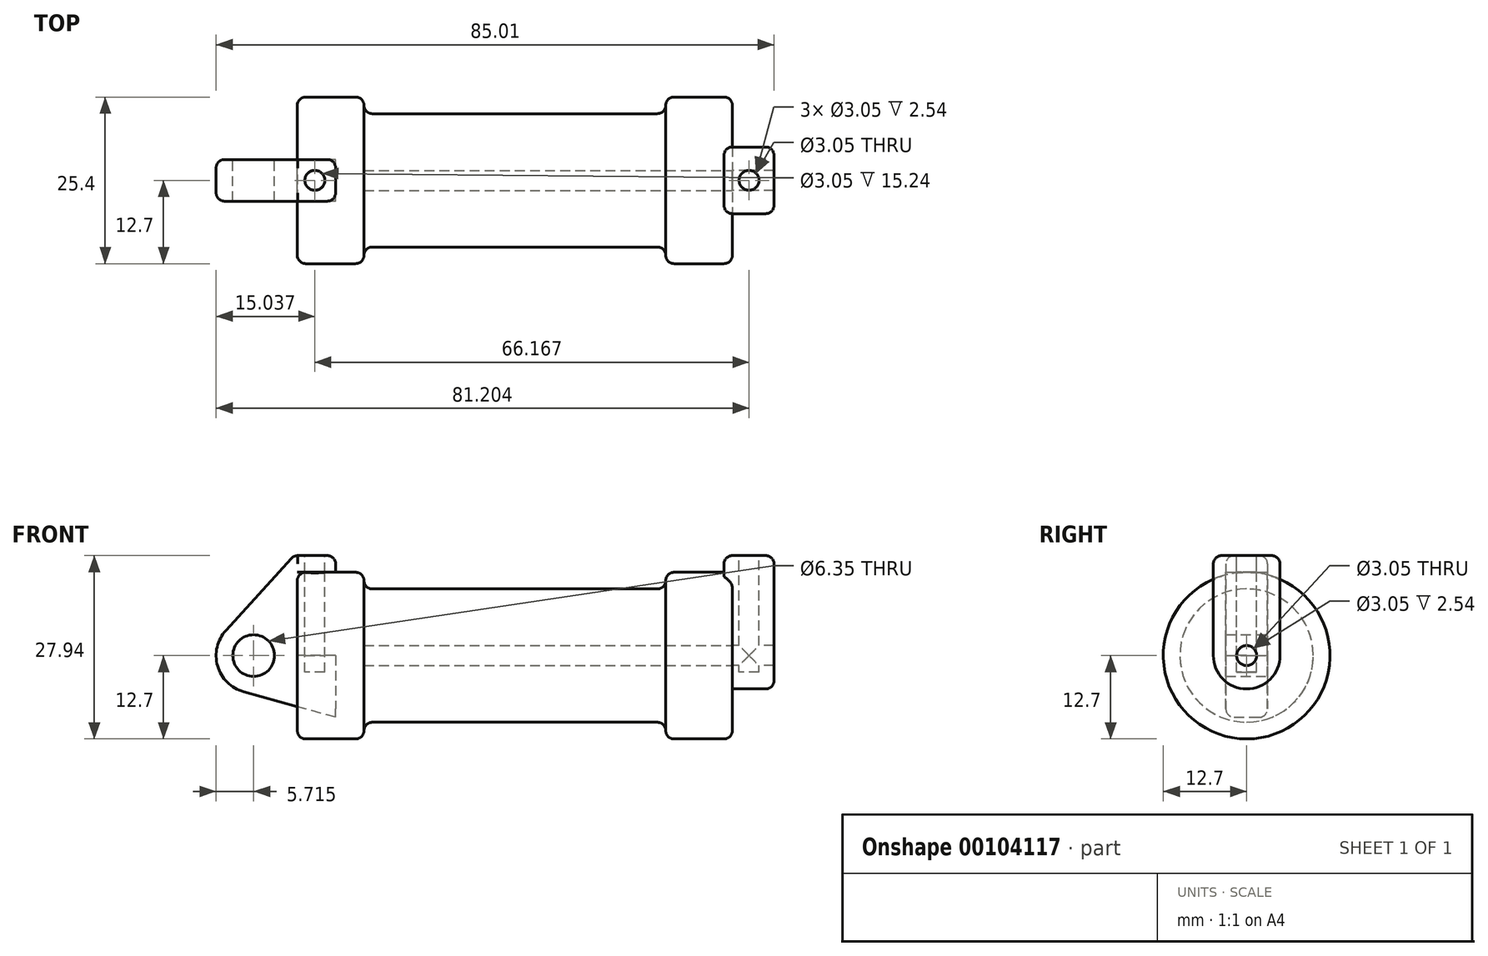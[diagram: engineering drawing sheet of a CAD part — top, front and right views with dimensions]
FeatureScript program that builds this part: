
annotation { "Feature Type Name" : "Feature", "Feature Type Description" : "" }
export const myFeature = defineFeature(function(context is Context, id is Id, definition is map)
    precondition{}
    {
        {
            var Q0;
            Q0=qCreatedBy(makeId("Front.planeOp"),FACE);
            var sketch = newSketch(context, id + "F0", { "sketchPlane" : qUnion([Q0])});
            skLineSegment(sketch, "E0", {"start": v(0, 0) * mm, "end": v(0, 12.7) * mm});
            skLineSegment(sketch, "E1", {"start": v(0, 12.7) * mm, "end": v(10.16, 12.7) * mm});
            skLineSegment(sketch, "E2", {"start": v(10.16, 12.7) * mm, "end": v(10.16, 10.16) * mm});
            skLineSegment(sketch, "E3", {"start": v(10.16, 10.16) * mm, "end": v(56.13, 10.16) * mm});
            skLineSegment(sketch, "E4", {"start": v(56.13, 10.16) * mm, "end": v(56.13, 12.7) * mm});
            skLineSegment(sketch, "E5", {"start": v(56.13, 12.7) * mm, "end": v(66.3, 12.7) * mm});
            skLineSegment(sketch, "E6", {"start": v(66.3, 12.7) * mm, "end": v(66.3, 0) * mm});
            skLineSegment(sketch, "E7", {"start": v(66.3, 0) * mm, "end": v(0, 0) * mm});
            skLineSegment(sketch, "E8", {"start": v(5.84, 15.24) * mm, "end": v(-0.5, 15.24) * mm});
            skLineSegment(sketch, "E9", {"start": v(-0.5, 15.24) * mm, "end": v(-10.88, 3.85) * mm});
            skLineSegment(sketch, "E10", {"start": v(0, 0) * mm, "end": v(-6.65, 0) * mm});
            skCircle(sketch, "E11", {"center": v(-6.65, 0) * mm, "radius": 5.72 * mm});
            skCircle(sketch, "E12", {"center": v(-6.65, 0) * mm, "radius": 3.18 * mm});
            skLineSegment(sketch, "E13", {"start": v(5.84, 15.24) * mm, "end": v(5.84, -9.4) * mm});
            skLineSegment(sketch, "E14", {"start": v(5.84, -9.4) * mm, "end": v(-8.18, -5.5) * mm});
            skSolve(sketch);
        }
        {
            var Q0;
            {var subQ0=sQuery(id+"F0.wireOp",EDGE,"E2");Q0=makeQuery(id+"F0.imprint","IMPRINT",FACE,{"disambiguationData":[TD([[makeQuery(id+"F0.imprint","IMPRINT",EDGE,{"derivedFrom":subQ0}),-1.0]])]});}
            var Q1;
            {var subQ0=sQuery(id+"F0.wireOp",EDGE,"E0");Q1=makeQuery(id+"F0.imprint","IMPRINT",FACE,{"disambiguationData":[TD([[makeQuery(id+"F0.imprint","IMPRINT",EDGE,{"derivedFrom":subQ0}),-1.0]])]});}
            var Q2;
            Q2=sQuery(id+"F0.wireOp",EDGE,"E7");
            revolve(context, id + "F1", {"entities" : qUnion([Q0, Q1]), "axis" : qUnion([Q2]), "revolveType" : RevolveType.FULL});
        }
        {
            var Q0;
            Q0=makeQuery(id+"F1.opRevolve","SWEPT_FACE",FACE,{"disambiguationData":[OSD([sQuery(id+"F0.wireOp",EDGE,"E6")])]});
            var sketch = newSketch(context, id + "F2", { "sketchPlane" : qUnion([Q0])});
            skCircle(sketch, "E15", {"center": v(0, 0) * mm, "radius": 1.52 * mm});
            skCircle(sketch, "E16", {"center": v(0, 0) * mm, "radius": 5.08 * mm});
            skLineSegment(sketch, "E17", {"start": v(-5.08, 0) * mm, "end": v(-5.08, 15.24) * mm});
            skLineSegment(sketch, "E18", {"start": v(5.08, 0) * mm, "end": v(5.08, 15.24) * mm});
            skLineSegment(sketch, "E19", {"start": v(-5.08, 15.24) * mm, "end": v(5.08, 15.24) * mm});
            skSolve(sketch);
        }
        {
            var Q0;
            {var subQ0=sQuery(id+"F2.wireOp",EDGE,"E19");Q0=makeQuery(id+"F2.imprint","IMPRINT",FACE,{"disambiguationData":[TD([[makeQuery(id+"F2.imprint","IMPRINT",EDGE,{"derivedFrom":subQ0}),-1.0]])]});}
            var Q1;
            Q1=makeQuery(id+"F2.imprint","IMPRINT",FACE,{"disambiguationData":[TD([[makeQuery(id+"F2.imprint","IMPRINT",EDGE,{"derivedFrom":sQuery(id+"F2.wireOp",EDGE,"E15")}),-1.0]])]});
            var Q2;
            {var subQ0=sQuery(id+"F2.wireOp",EDGE,"E17");var subQ1=sQuery(id+"F2.wireOp",EDGE,"E16");var subQ2=makeQuery(id+"F2.imprint","INTERSECT",VERTEX,{"derivedFrom":[subQ1,subQ0]});Q2=makeQuery(id+"F2.imprint","IMPRINT",FACE,{"disambiguationData":[TD([[makeQuery(id+"F2.imprint","IMPRINT",EDGE,{"disambiguationData":[TD([[subQ2,1.0]])],"derivedFrom":subQ1}),-1.0]])]});}
            extrude(context, id + "F3", {"entities" : qUnion([Q0, Q1, Q2]), "operationType" : NewBodyOperationType.ADD, "oppositeDirection" : true, "depth" : 1.27 * mm});
        }
        {
            var Q0;
            Q0 = qSketchRegion(id + "F2", true);
            extrude(context, id + "F4", {"entities" : qUnion([Q0]), "operationType" : NewBodyOperationType.ADD, "depth" : 6.35 * mm});
        }
        {
            var Q0;
            {var subQ0=sQuery(id+"F2.wireOp",EDGE,"E15");Q0=makeQuery(id+"F4.boolean.opBoolean","SPLIT",FACE,{"disambiguationData":[TD([makeQuery(id+"F4.opExtrude","SWEPT_FACE",FACE,{"disambiguationData":[OSD([subQ0])]})])],"derivedFrom":makeQuery(id+"F3.boolean.opBoolean","MERGE",FACE,{"derivedFrom":[makeQuery(id+"F1.opRevolve","SWEPT_FACE",FACE,{"disambiguationData":[OSD([sQuery(id+"F0.wireOp",EDGE,"E6")])]}),makeQuery(id+"F3.opExtrude","CAP_FACE",FACE,{"disambiguationData":[OSD([subQ0,sQuery(id+"F2.wireOp",EDGE,"E16"),sQuery(id+"F2.wireOp",EDGE,"E17"),sQuery(id+"F2.wireOp",EDGE,"E18"),sQuery(id+"F2.wireOp",EDGE,"E19")])],"isStart":true})]})});}
            var Q1;
            Q1=makeQuery(id+"F1.opRevolve","SWEPT_FACE",FACE,{"disambiguationData":[OSD([sQuery(id+"F0.wireOp",EDGE,"E2")])]});
            extrude(context, id + "F5", {"entities" : qUnion([Q0]), "endBound" : BoundingType.UP_TO_SURFACE, "oppositeDirection" : true, "endBoundEntityFace" : qUnion([Q1]), "depth" : 25.4 * mm});
        }
        {
            var Q0;
            {var subQ0=sQuery(id+"F2.wireOp",EDGE,"E19");Q0=makeQuery(id+"F4.boolean.opBoolean","MERGE",FACE,{"derivedFrom":[makeQuery(id+"F3.opExtrude","SWEPT_FACE",FACE,{"disambiguationData":[OSD([subQ0])]}),makeQuery(id+"F4.opExtrude","SWEPT_FACE",FACE,{"disambiguationData":[OSD([subQ0])]})]});}
            var sketch = newSketch(context, id + "F6", { "sketchPlane" : qUnion([Q0])});
            skLineSegment(sketch, "E20", {"start": v(65.02, 5.08) * mm, "end": v(72.64, -5.08) * mm, "construction": true});
            skLineSegment(sketch, "E21", {"start": v(65.02, -5.08) * mm, "end": v(72.64, 5.08) * mm, "construction": true});
            skCircle(sketch, "E22", {"center": v(68.83, 0) * mm, "radius": 1.52 * mm});
            skSolve(sketch);
        }
        {
            var Q0;
            Q0 = qSketchRegion(id + "F6", true);
            extrude(context, id + "F7", {"entities" : qUnion([Q0]), "operationType" : NewBodyOperationType.REMOVE, "oppositeDirection" : true, "depth" : 17.78 * mm});
        }
        {
            var Q0;
            {var subQ3=sQuery(id+"F0.wireOp",EDGE,"E0");Q0=makeQuery(id+"F0.imprint","IMPRINT",FACE,{"disambiguationData":[TD([[makeQuery(id+"F0.imprint","IMPRINT",EDGE,{"derivedFrom":subQ3}),1.0]])]});}
            var Q1;
            {var subQ0=sQuery(id+"F0.wireOp",EDGE,"E14");Q1=makeQuery(id+"F0.imprint","IMPRINT",FACE,{"disambiguationData":[TD([[makeQuery(id+"F0.imprint","IMPRINT",EDGE,{"derivedFrom":subQ0}),-1.0]])]});}
            var Q2;
            {var subQ4=sQuery(id+"F0.wireOp",EDGE,"E12");Q2=makeQuery(id+"F0.imprint","IMPRINT",FACE,{"disambiguationData":[TD([[makeQuery(id+"F0.imprint","IMPRINT",EDGE,{"derivedFrom":subQ4}),-1.0]])]});}
            extrude(context, id + "F8", {"entities" : qUnion([Q0, Q1, Q2]), "endBound" : BoundingType.SYMMETRIC, "depth" : 6.35 * mm});
        }
        {
            var Q0;
            Q0=makeQuery(id+"F8.opExtrude","SWEPT_FACE",FACE,{"disambiguationData":[OSD([sQuery(id+"F0.wireOp",EDGE,"E8")])]});
            var sketch = newSketch(context, id + "F9", { "sketchPlane" : qUnion([Q0])});
            skCircle(sketch, "E23", {"center": v(2.67, 0) * mm, "radius": 1.52 * mm});
            skPoint(sketch, "E23.centerSnap0", {"position": v(-0.5, 0) * mm});
            skPoint(sketch, "E23.centerSnap1", {"position": v(2.67, 3.18) * mm});
            skSolve(sketch);
        }
        {
            var Q0;
            Q0=makeQuery(id+"F9.imprint","IMPRINT",FACE,{"disambiguationData":[TD([[makeQuery(id+"F9.imprint","IMPRINT",EDGE,{"derivedFrom":sQuery(id+"F9.wireOp",EDGE,"E23")}),1.0]])]});
            var Q1;
            Q1=sQuery(id+"F9.wireOp",EDGE,"E23");
            extrude(context, id + "F10", {"entities" : qUnion([Q0]), "operationType" : NewBodyOperationType.REMOVE, "surfaceEntities" : qUnion([Q1]), "oppositeDirection" : true, "depth" : 17.78 * mm});
        }
        {
            var Q0;
            Q0=makeQuery(id+"F1.opRevolve","SWEPT_EDGE",EDGE,{"disambiguationData":[OSD([sQuery(id+"F0.wireOp",EDGE,"E4"),sQuery(id+"F0.wireOp",EDGE,"E5")])]});
            var Q1;
            Q1=makeQuery(id+"F1.opRevolve","SWEPT_EDGE",EDGE,{"disambiguationData":[OSD([sQuery(id+"F0.wireOp",EDGE,"E5"),sQuery(id+"F0.wireOp",EDGE,"E6")])]});
            fillet(context, id + "F11", {"entities" : qUnion([Q0, Q1]), "radius" : 1.27 * mm, "tangentPropagation" : true, "allowEdgeOverflow" : false});
        }
        {
            var Q0;
            Q0=makeQuery(id+"F1.opRevolve","SWEPT_EDGE",EDGE,{"disambiguationData":[OSD([sQuery(id+"F0.wireOp",EDGE,"E3"),sQuery(id+"F0.wireOp",EDGE,"E4")])]});
            fillet(context, id + "F12", {"entities" : qUnion([Q0]), "radius" : 1.27 * mm, "tangentPropagation" : true, "allowEdgeOverflow" : false});
        }
        {
            var Q0;
            Q0=makeQuery(id+"F1.opRevolve","SWEPT_EDGE",EDGE,{"disambiguationData":[OSD([sQuery(id+"F0.wireOp",EDGE,"E1"),sQuery(id+"F0.wireOp",EDGE,"E2")])]});
            fillet(context, id + "F13", {"entities" : qUnion([Q0]), "radius" : 1.27 * mm, "tangentPropagation" : true, "allowEdgeOverflow" : false});
        }
        {
            var Q0;
            Q0=makeQuery(id+"F1.opRevolve","SWEPT_EDGE",EDGE,{"disambiguationData":[OSD([sQuery(id+"F0.wireOp",EDGE,"E2"),sQuery(id+"F0.wireOp",EDGE,"E3")])]});
            fillet(context, id + "F14", {"entities" : qUnion([Q0]), "radius" : 1.27 * mm, "tangentPropagation" : true, "allowEdgeOverflow" : false});
        }
        {
            var Q0;
            Q0=makeQuery(id+"F8.opExtrude","CAP_EDGE",EDGE,{"disambiguationData":[OSD([sQuery(id+"F0.wireOp",EDGE,"E8")])],"isStart":true});
            var Q1;
            Q1=makeQuery(id+"F8.opExtrude","CAP_EDGE",EDGE,{"disambiguationData":[OSD([sQuery(id+"F0.wireOp",EDGE,"E8")])],"isStart":false});
            fillet(context, id + "F15", {"entities" : qUnion([Q0, Q1]), "radius" : 1.27 * mm, "tangentPropagation" : true, "allowEdgeOverflow" : false});
        }
        {
            var Q0;
            Q0=makeQuery(id+"F8.opExtrude","CAP_EDGE",EDGE,{"disambiguationData":[OSD([sQuery(id+"F0.wireOp",EDGE,"E11")])],"isStart":false});
            var Q1;
            Q1=makeQuery(id+"F8.opExtrude","CAP_EDGE",EDGE,{"disambiguationData":[OSD([sQuery(id+"F0.wireOp",EDGE,"E11")])],"isStart":true});
            fillet(context, id + "F16", {"entities" : qUnion([Q0, Q1]), "radius" : 1.27 * mm, "tangentPropagation" : true, "allowEdgeOverflow" : false});
        }
        {
            var Q0;
            Q0=makeQuery(id+"F1.opRevolve","SWEPT_EDGE",EDGE,{"disambiguationData":[OSD([sQuery(id+"F0.wireOp",EDGE,"E0"),sQuery(id+"F0.wireOp",EDGE,"E1")])]});
            fillet(context, id + "F17", {"entities" : qUnion([Q0]), "radius" : 1.27 * mm, "tangentPropagation" : true, "allowEdgeOverflow" : false});
        }
        {
            var Q0;
            Q0=makeQuery(id+"F8.opExtrude","SWEPT_EDGE",EDGE,{"disambiguationData":[OSD([sQuery(id+"F0.wireOp",EDGE,"E8"),sQuery(id+"F0.wireOp",EDGE,"E13")])]});
            fillet(context, id + "F18", {"entities" : qUnion([Q0]), "radius" : 1.27 * mm, "tangentPropagation" : true, "allowEdgeOverflow" : false});
        }
        {
            var Q0;
            {var subQ0=sQuery(id+"F2.wireOp",EDGE,"E19");var subQ1=sQuery(id+"F2.wireOp",EDGE,"E17");Q0=makeQuery(id+"F4.boolean.opBoolean","MERGE",EDGE,{"derivedFrom":[makeQuery(id+"F3.opExtrude","SWEPT_EDGE",EDGE,{"disambiguationData":[OSD([subQ1,subQ0])]}),makeQuery(id+"F4.opExtrude","SWEPT_EDGE",EDGE,{"disambiguationData":[OSD([subQ1,subQ0])]})]});}
            var Q1;
            {var subQ0=sQuery(id+"F2.wireOp",EDGE,"E19");var subQ1=sQuery(id+"F2.wireOp",EDGE,"E18");Q1=makeQuery(id+"F4.boolean.opBoolean","MERGE",EDGE,{"derivedFrom":[makeQuery(id+"F3.opExtrude","SWEPT_EDGE",EDGE,{"disambiguationData":[OSD([subQ1,subQ0])]}),makeQuery(id+"F4.opExtrude","SWEPT_EDGE",EDGE,{"disambiguationData":[OSD([subQ1,subQ0])]})]});}
            fillet(context, id + "F19", {"entities" : qUnion([Q0, Q1]), "radius" : 1.27 * mm, "tangentPropagation" : true, "allowEdgeOverflow" : false});
        }
        {
            var Q0;
            Q0=makeQuery(id+"F4.opExtrude","CAP_EDGE",EDGE,{"disambiguationData":[OSD([sQuery(id+"F2.wireOp",EDGE,"E19")])],"isStart":false});
            fillet(context, id + "F20", {"entities" : qUnion([Q0]), "radius" : 1.27 * mm, "tangentPropagation" : true, "allowEdgeOverflow" : false});
        }
        {
            var Q0;
            Q0=makeQuery(id+"F3.opExtrude","CAP_EDGE",EDGE,{"disambiguationData":[OSD([sQuery(id+"F2.wireOp",EDGE,"E19")])],"isStart":false});
            fillet(context, id + "F21", {"entities" : qUnion([Q0]), "radius" : 1.27 * mm, "tangentPropagation" : true, "allowEdgeOverflow" : false});
        }
    });
